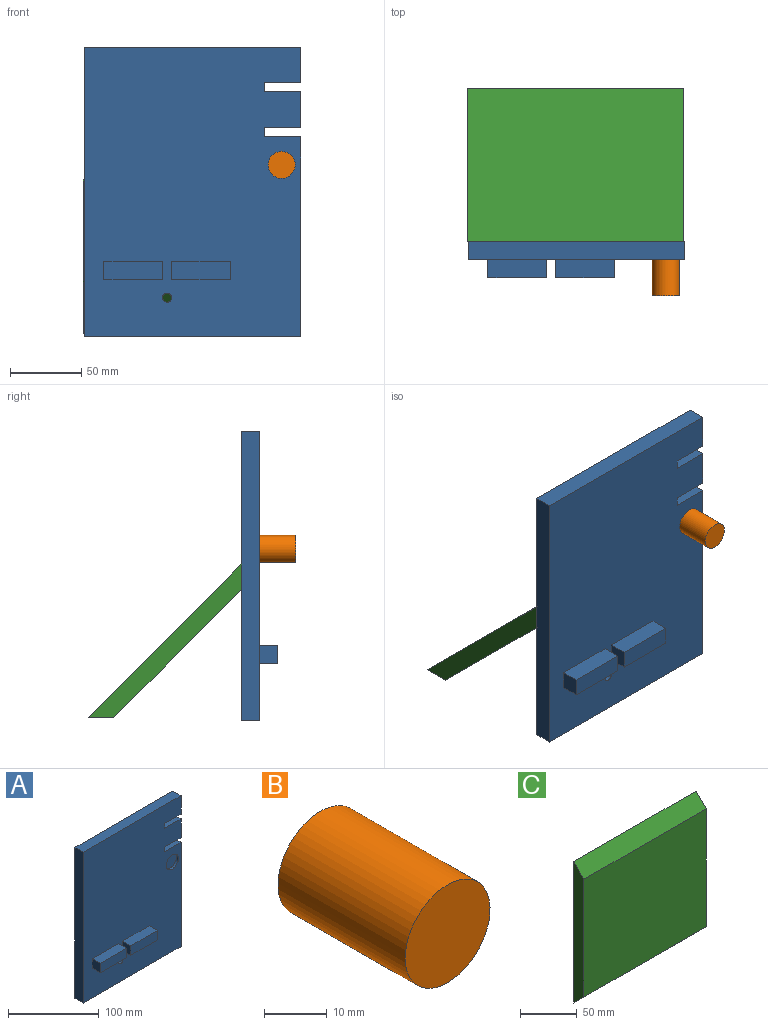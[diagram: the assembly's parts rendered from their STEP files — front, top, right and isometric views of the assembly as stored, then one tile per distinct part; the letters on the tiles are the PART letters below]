
ASSEMBLY  parts=3 mates=2
PART A: 27 faces, bbox 152.4x25.4x203.2 mm
  f0: plane 203.2x152.4mm, normal (0,-1,0), area 29280mm2, adj f1,f2,f3,f4,f5,f6,f7,f8
  f1: plane 203.2x12.7mm, normal (-1,0,0), area 2580.6mm2, adj f0,f2,f12,f13
  f2: plane 152.4x12.7mm, normal (0,0,-1), area 1935.5mm2, adj f0,f1,f3,f13
  f3: plane 140.3x12.7mm, normal (1,0,0), area 1781.8mm2, adj f0,f2,f4,f13
  f4: plane 25.4x12.7mm, normal (0,0,1), area 322.6mm2, adj f0,f3,f5,f13
  f5: plane 12.7x6.35mm, normal (1,0,0), area 80.6mm2, adj f0,f4,f6,f13
  f6: plane 25.4x12.7mm, normal (0,0,-1), area 322.6mm2, adj f0,f5,f7,f13
  f7: plane 25.4x12.7mm, normal (1,0,0), area 322.6mm2, adj f0,f6,f8,f13
  f8: plane 25.4x12.7mm, normal (0,0,1), area 322.6mm2, adj f0,f7,f9,f13
  f9: plane 12.7x6.35mm, normal (1,0,0), area 80.6mm2, adj f0,f8,f10,f13
  f10: plane 25.4x12.7mm, normal (0,0,-1), area 322.6mm2, adj f0,f9,f11,f13
  f11: plane 24.8x12.7mm, normal (1,0,0), area 315mm2, adj f0,f10,f12,f13
  f12: plane 152.4x12.7mm, normal (0,0,1), area 1935.5mm2, adj f0,f1,f11,f13
  f13: plane 203.2x152.4mm, normal (0,1,0), area 30613.4mm2, adj f1,f2,f3,f4,f5,f6,f7,f8
  f14: cylinder r=9.53mm len=19.05mm, axis (0,-1,0), area 190mm2, adj f0,f15
  f15: plane 19.05x19.05mm, normal (0,-1,0), area 285mm2, adj f14
  f16: plane 41.28x12.7mm, normal (0,0,1), area 524.2mm2, adj f0,f17,f19,f20
  f17: plane 12.7x12.7mm, normal (-1,0,0), area 161.3mm2, adj f0,f16,f18,f20
  f18: plane 41.28x12.7mm, normal (0,0,-1), area 524.2mm2, adj f0,f17,f19,f20
  f19: plane 12.7x12.7mm, normal (1,0,0), area 161.3mm2, adj f0,f16,f18,f20
  f20: plane 41.28x12.7mm, normal (0,-1,0), area 524.2mm2, adj f16,f17,f18,f19
  f21: plane 12.7x12.7mm, normal (1,0,0), area 161.3mm2, adj f0,f22,f24,f25
  f22: plane 41.28x12.7mm, normal (0,0,1), area 524.2mm2, adj f0,f21,f23,f25
  f23: plane 12.7x12.7mm, normal (-1,0,0), area 161.3mm2, adj f0,f22,f24,f25
  f24: plane 41.28x12.7mm, normal (0,0,-1), area 524.2mm2, adj f0,f21,f23,f25
  f25: plane 41.28x12.7mm, normal (0,-1,0), area 524.2mm2, adj f21,f22,f23,f24
  f26: cylinder r=3.17mm len=12.7mm, axis (0,-1,0), area 253.4mm2, adj f0,f13
PART B: 3 faces, bbox 19.1x28.6x19.1 mm
  f0: cylinder r=9.53mm len=28.58mm, axis (0,1,0), area 1710.1mm2, adj f1,f2
  f1: plane 19.05x19.05mm, normal (0,-1,0), area 285mm2, adj f0
  f2: plane 19.05x19.05mm, normal (0,1,0), area 285mm2, adj f0
PART C: 6 faces, bbox 152.4x12.7x152.4 mm
  f0: plane 152.4x12.7mm, normal (-1,0,0), area 1774.2mm2, adj f2,f3,f4,f5
  f1: plane 152.4x12.7mm, normal (1,0,0), area 1774.2mm2, adj f2,f3,f4,f5
  f2: plane 152.4x127mm, normal (0,-1,0), area 19354.8mm2, adj f0,f1,f4,f5
  f3: plane 152.4x152.4mm, normal (0,1,0), area 23225.8mm2, adj f0,f1,f4,f5
  f4: plane 152.4x12.7mm, normal (0,-0.71,0.71), area 2737.2mm2, adj f0,f1,f2,f3
  f5: plane 152.4x12.7mm, normal (0,-0.71,-0.71), area 2737.2mm2, adj f0,f1,f2,f3
PLACE A t=(-3.77,-35.92,26.26)mm
PLACE B t=(58.9,-45.45,45.28)mm
PLACE C rot(axis=(1,0,0),45deg) t=(-80.62,27.52,-28.73)mm
MATE fastened C.f4 <-> A.f13  axis (0,-1,0) through (-4.42,-35.92,25.73)mm
MATE fastened B.f0 <-> A.f14  axis (0,1,0) through (58.9,-45.45,45.28)mm
